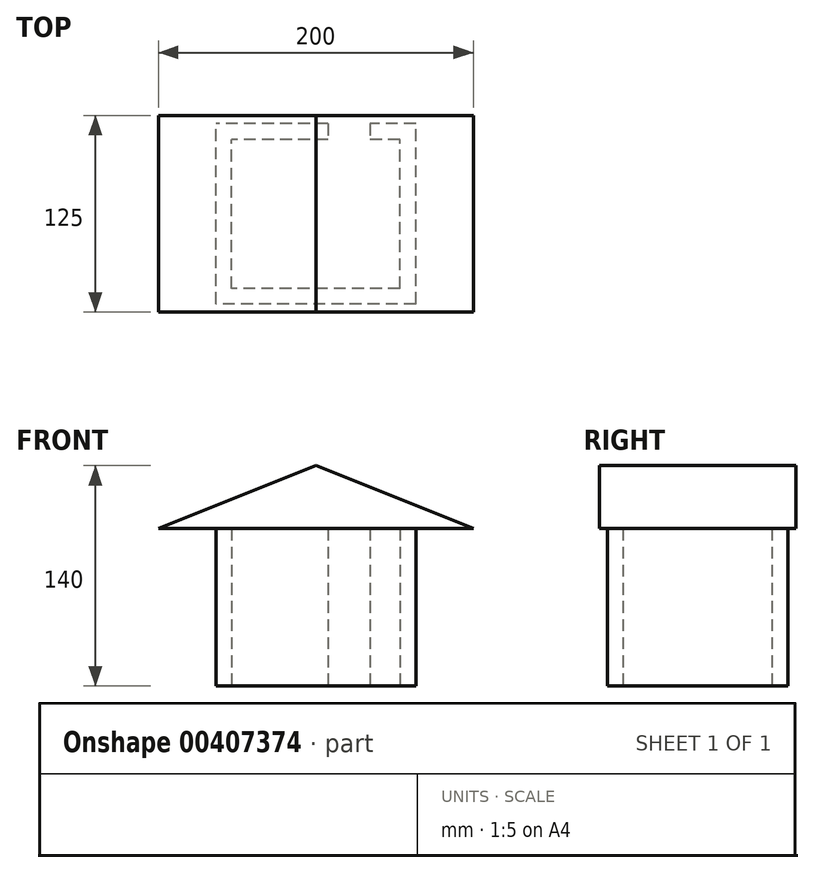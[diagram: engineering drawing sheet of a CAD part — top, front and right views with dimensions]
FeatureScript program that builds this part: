
annotation { "Feature Type Name" : "Feature", "Feature Type Description" : "" }
export const myFeature = defineFeature(function(context is Context, id is Id, definition is map)
    precondition{}
    {
        {
            var Q0;
            Q0=qCreatedBy(makeId("Top.planeOp"),FACE);
            var sketch = newSketch(context, id + "F0", { "sketchPlane" : qUnion([Q0])});
            skLineSegment(sketch, "E0.bottom", {"start": v(53.49, -47.3) * mm, "end": v(-53.49, -47.3) * mm});
            skLineSegment(sketch, "E0.top", {"start": v(53.49, 47.3) * mm, "end": v(34.41, 47.3) * mm});
            skLineSegment(sketch, "E0.left", {"start": v(53.49, -47.3) * mm, "end": v(53.49, 47.3) * mm});
            skLineSegment(sketch, "E0.right", {"start": v(-53.49, -47.3) * mm, "end": v(-53.49, 47.3) * mm});
            skPoint(sketch, "E0.middle", {"position": v(0, 0) * mm});
            skLineSegment(sketch, "E1.bottom", {"start": v(63.49, -57.3) * mm, "end": v(-63.49, -57.3) * mm});
            skLineSegment(sketch, "E1.top", {"start": v(63.49, 57.3) * mm, "end": v(34.41, 57.3) * mm});
            skLineSegment(sketch, "E1.left", {"start": v(63.49, -57.3) * mm, "end": v(63.49, 57.3) * mm});
            skLineSegment(sketch, "E1.right", {"start": v(-63.49, -57.3) * mm, "end": v(-63.49, 57.3) * mm});
            skLineSegment(sketch, "E2", {"start": v(34.41, 57.3) * mm, "end": v(34.41, 47.3) * mm});
            skLineSegment(sketch, "E3", {"start": v(7.84, 57.3) * mm, "end": v(7.84, 47.3) * mm});
            skLineSegment(sketch, "E4.trimOffspring", {"start": v(7.84, 47.3) * mm, "end": v(-53.49, 47.3) * mm});
            skLineSegment(sketch, "E5.trimOffspring", {"start": v(7.84, 57.3) * mm, "end": v(-63.49, 57.3) * mm});
            skSolve(sketch);
        }
        {
            var Q0;
            Q0 = qSketchRegion(id + "F0", true);
            extrude(context, id + "F1", {"entities" : qUnion([Q0]), "depth" : 100 * mm});
        }
        {
            var Q0;
            Q0=qCreatedBy(makeId("Front.planeOp"),FACE);
            var sketch = newSketch(context, id + "F2", { "sketchPlane" : qUnion([Q0])});
            skLineSegment(sketch, "E6", {"start": v(0, 140) * mm, "end": v(100, 100) * mm});
            skLineSegment(sketch, "E7", {"start": v(100, 100) * mm, "end": v(-100, 100) * mm});
            skLineSegment(sketch, "E8", {"start": v(-100, 100) * mm, "end": v(0, 140) * mm});
            skLineSegment(sketch, "E9", {"start": v(0, 140) * mm, "end": v(0, 100) * mm, "construction": true});
            skSolve(sketch);
        }
        {
            var Q0;
            Q0=makeQuery(id+"F2.imprint","IMPRINT",FACE,{"disambiguationData":[TD([[makeQuery(id+"F2.imprint","IMPRINT",EDGE,{"derivedFrom":sQuery(id+"F2.wireOp",EDGE,"E6")}),-1.0]])]});
            extrude(context, id + "F3", {"entities" : qUnion([Q0]), "endBound" : BoundingType.SYMMETRIC, "depth" : 125 * mm});
        }
    });
